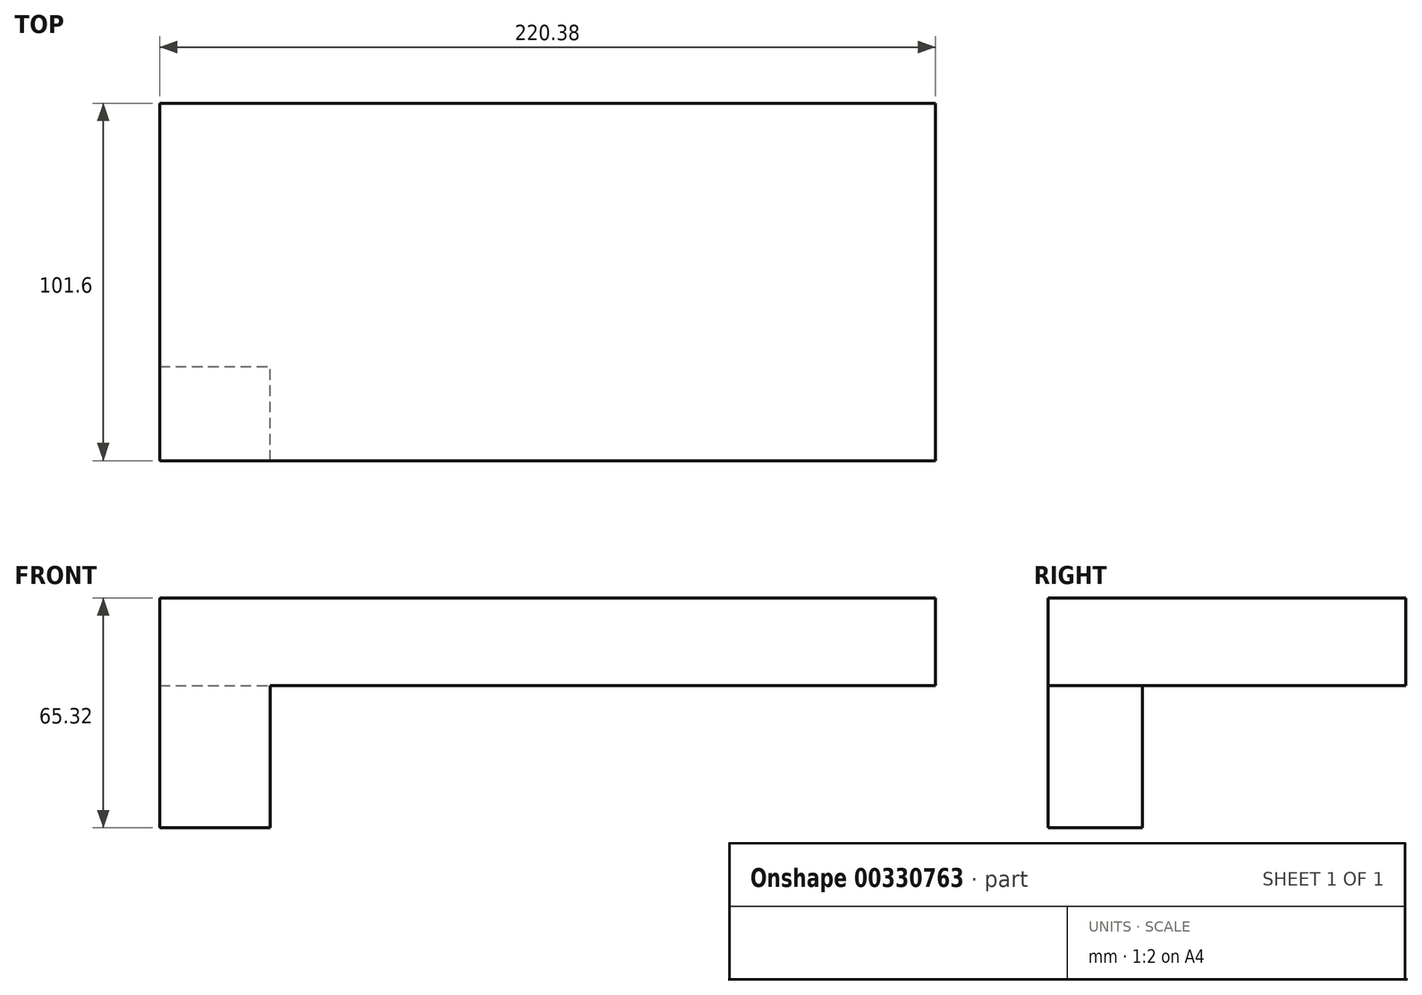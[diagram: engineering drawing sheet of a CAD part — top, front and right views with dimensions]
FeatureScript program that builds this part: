
annotation { "Feature Type Name" : "Feature", "Feature Type Description" : "" }
export const myFeature = defineFeature(function(context is Context, id is Id, definition is map)
    precondition{}
    {
        {
            var Q0;
            Q0=qCreatedBy(makeId("Front.planeOp"),FACE);
            var sketch = newSketch(context, id + "F0", { "sketchPlane" : qUnion([Q0])});
            skLineSegment(sketch, "E0.bottom", {"start": v(59.4, 12.46) * mm, "end": v(-59.4, 12.46) * mm});
            skLineSegment(sketch, "E0.top", {"start": v(59.4, -12.46) * mm, "end": v(-59.4, -12.46) * mm});
            skLineSegment(sketch, "E0.left", {"start": v(59.4, 12.46) * mm, "end": v(59.4, -12.46) * mm});
            skLineSegment(sketch, "E0.right", {"start": v(-59.4, 12.46) * mm, "end": v(-59.4, -12.46) * mm});
            skPoint(sketch, "E0.middle", {"position": v(0, 0) * mm});
            skSolve(sketch);
        }
        {
            var Q0;
            Q0=makeQuery(id+"F0.imprint","IMPRINT",FACE,{"disambiguationData":[TD([[makeQuery(id+"F0.imprint","IMPRINT",EDGE,{"derivedFrom":sQuery(id+"F0.wireOp",EDGE,"E0.bottom")}),1.0]])]});
            extrude(context, id + "F1", {"entities" : qUnion([Q0]), "depth" : 25.4 * mm});
        }
        {
            var Q0;
            Q0=makeQuery(id+"F1.opExtrude","CAP_FACE",FACE,{"disambiguationData":[OSD([sQuery(id+"F0.wireOp",EDGE,"E0.bottom"),sQuery(id+"F0.wireOp",EDGE,"E0.top"),sQuery(id+"F0.wireOp",EDGE,"E0.left"),sQuery(id+"F0.wireOp",EDGE,"E0.right")])],"isStart":true});
            extrude(context, id + "F2", {"entities" : qUnion([Q0]), "operationType" : NewBodyOperationType.ADD, "depth" : 25.4 * mm});
        }
        {
            var Q0;
            {var subQ0=sQuery(id+"F0.wireOp",EDGE,"E0.right");Q0=makeQuery(id+"F2.boolean.opBoolean","MERGE",FACE,{"derivedFrom":[makeQuery(id+"F1.opExtrude","SWEPT_FACE",FACE,{"disambiguationData":[OSD([subQ0])]}),makeQuery(id+"F2.opExtrude","SWEPT_FACE",FACE,{"disambiguationData":[OSD([subQ0])]})]});}
            extrude(context, id + "F3", {"entities" : qUnion([Q0]), "operationType" : NewBodyOperationType.ADD, "depth" : 25.4 * mm});
        }
        {
            var Q0;
            {var subQ0=sQuery(id+"F0.wireOp",EDGE,"E0.left");Q0=makeQuery(id+"F2.boolean.opBoolean","MERGE",FACE,{"derivedFrom":[makeQuery(id+"F1.opExtrude","SWEPT_FACE",FACE,{"disambiguationData":[OSD([subQ0])]}),makeQuery(id+"F2.opExtrude","SWEPT_FACE",FACE,{"disambiguationData":[OSD([subQ0])]})]});}
            extrude(context, id + "F4", {"entities" : qUnion([Q0]), "operationType" : NewBodyOperationType.ADD, "depth" : 25.4 * mm});
        }
        {
            var Q0;
            Q0=makeQuery(id+"F4.opExtrude","CAP_FACE",FACE,{"disambiguationData":[OSD([sQuery(id+"F0.wireOp",EDGE,"E0.left")])],"isStart":false});
            extrude(context, id + "F5", {"entities" : qUnion([Q0]), "operationType" : NewBodyOperationType.ADD, "depth" : 25.4 * mm});
        }
        {
            var Q0;
            Q0=makeQuery(id+"F3.opExtrude","CAP_FACE",FACE,{"disambiguationData":[OSD([sQuery(id+"F0.wireOp",EDGE,"E0.right")])],"isStart":false});
            extrude(context, id + "F6", {"entities" : qUnion([Q0]), "operationType" : NewBodyOperationType.ADD, "depth" : 25.4 * mm});
        }
        {
            var Q0;
            {var subQ0=sQuery(id+"F0.wireOp",EDGE,"E0.right");var subQ1=makeQuery(id+"F1.opExtrude","CAP_EDGE",EDGE,{"disambiguationData":[OSD([subQ0])],"isStart":false});var subQ2=sQuery(id+"F0.wireOp",EDGE,"E0.left");var subQ3=makeQuery(id+"F1.opExtrude","CAP_EDGE",EDGE,{"disambiguationData":[OSD([subQ2])],"isStart":false});Q0=makeQuery(id+"F6.boolean.opBoolean","MERGE",FACE,{"derivedFrom":[makeQuery(id+"F5.boolean.opBoolean","MERGE",FACE,{"derivedFrom":[makeQuery(id+"F4.boolean.opBoolean","MERGE",FACE,{"derivedFrom":[makeQuery(id+"F3.boolean.opBoolean","MERGE",FACE,{"derivedFrom":[makeQuery(id+"F1.opExtrude","CAP_FACE",FACE,{"disambiguationData":[OSD([sQuery(id+"F0.wireOp",EDGE,"E0.bottom"),sQuery(id+"F0.wireOp",EDGE,"E0.top"),subQ2,subQ0])],"isStart":false}),makeQuery(id+"F3.opExtrude","SWEPT_FACE",FACE,{"disambiguationData":[OSD([subQ0]),TDD([subQ1])]})]}),makeQuery(id+"F4.opExtrude","SWEPT_FACE",FACE,{"disambiguationData":[OSD([subQ2]),TDD([subQ3])]})]}),makeQuery(id+"F5.opExtrude","SWEPT_FACE",FACE,{"disambiguationData":[OSD([subQ2]),TDD([makeQuery(id+"F4.opExtrude","CAP_EDGE",EDGE,{"disambiguationData":[OSD([subQ2]),TDD([subQ3])],"isStart":false})])]})]}),makeQuery(id+"F6.opExtrude","SWEPT_FACE",FACE,{"disambiguationData":[OSD([subQ0]),TDD([makeQuery(id+"F3.opExtrude","CAP_EDGE",EDGE,{"disambiguationData":[OSD([subQ0]),TDD([subQ1])],"isStart":false})])]})]});}
            extrude(context, id + "F7", {"entities" : qUnion([Q0]), "operationType" : NewBodyOperationType.ADD, "depth" : 25.4 * mm});
        }
        {
            var Q0;
            {var subQ0=sQuery(id+"F0.wireOp",EDGE,"E0.right");var subQ1=makeQuery(id+"F2.opExtrude","CAP_EDGE",EDGE,{"disambiguationData":[OSD([subQ0])],"isStart":false});var subQ2=sQuery(id+"F0.wireOp",EDGE,"E0.left");var subQ3=makeQuery(id+"F2.opExtrude","CAP_EDGE",EDGE,{"disambiguationData":[OSD([subQ2])],"isStart":false});Q0=makeQuery(id+"F6.boolean.opBoolean","MERGE",FACE,{"derivedFrom":[makeQuery(id+"F5.boolean.opBoolean","MERGE",FACE,{"derivedFrom":[makeQuery(id+"F4.boolean.opBoolean","MERGE",FACE,{"derivedFrom":[makeQuery(id+"F3.boolean.opBoolean","MERGE",FACE,{"derivedFrom":[makeQuery(id+"F2.opExtrude","CAP_FACE",FACE,{"disambiguationData":[OSD([sQuery(id+"F0.wireOp",EDGE,"E0.bottom"),sQuery(id+"F0.wireOp",EDGE,"E0.top"),subQ2,subQ0])],"isStart":false}),makeQuery(id+"F3.opExtrude","SWEPT_FACE",FACE,{"disambiguationData":[OSD([subQ0]),TDD([subQ1])]})]}),makeQuery(id+"F4.opExtrude","SWEPT_FACE",FACE,{"disambiguationData":[OSD([subQ2]),TDD([subQ3])]})]}),makeQuery(id+"F5.opExtrude","SWEPT_FACE",FACE,{"disambiguationData":[OSD([subQ2]),TDD([makeQuery(id+"F4.opExtrude","CAP_EDGE",EDGE,{"disambiguationData":[OSD([subQ2]),TDD([subQ3])],"isStart":false})])]})]}),makeQuery(id+"F6.opExtrude","SWEPT_FACE",FACE,{"disambiguationData":[OSD([subQ0]),TDD([makeQuery(id+"F3.opExtrude","CAP_EDGE",EDGE,{"disambiguationData":[OSD([subQ0]),TDD([subQ1])],"isStart":false})])]})]});}
            extrude(context, id + "F8", {"entities" : qUnion([Q0]), "operationType" : NewBodyOperationType.ADD, "depth" : 25.4 * mm});
        }
        {
            var Q0;
            {var subQ0=sQuery(id+"F0.wireOp",EDGE,"E0.right");var subQ1=sQuery(id+"F0.wireOp",EDGE,"E0.left");var subQ2=sQuery(id+"F0.wireOp",EDGE,"E0.bottom");Q0=makeQuery(id+"F8.boolean.opBoolean","MERGE",FACE,{"derivedFrom":[makeQuery(id+"F7.boolean.opBoolean","MERGE",FACE,{"derivedFrom":[makeQuery(id+"F6.boolean.opBoolean","MERGE",FACE,{"derivedFrom":[makeQuery(id+"F5.boolean.opBoolean","MERGE",FACE,{"derivedFrom":[makeQuery(id+"F4.boolean.opBoolean","MERGE",FACE,{"derivedFrom":[makeQuery(id+"F3.boolean.opBoolean","MERGE",FACE,{"derivedFrom":[makeQuery(id+"F2.boolean.opBoolean","MERGE",FACE,{"derivedFrom":[makeQuery(id+"F1.opExtrude","SWEPT_FACE",FACE,{"disambiguationData":[OSD([subQ2])]}),makeQuery(id+"F2.opExtrude","SWEPT_FACE",FACE,{"disambiguationData":[OSD([subQ2])]})]}),makeQuery(id+"F3.opExtrude","SWEPT_FACE",FACE,{"disambiguationData":[OSD([subQ2,subQ0])]})]}),makeQuery(id+"F4.opExtrude","SWEPT_FACE",FACE,{"disambiguationData":[OSD([subQ2,subQ1])]})]}),makeQuery(id+"F5.opExtrude","SWEPT_FACE",FACE,{"disambiguationData":[OSD([subQ2,subQ1])]})]}),makeQuery(id+"F6.opExtrude","SWEPT_FACE",FACE,{"disambiguationData":[OSD([subQ2,subQ0])]})]}),makeQuery(id+"F7.opExtrude","SWEPT_FACE",FACE,{"disambiguationData":[OSD([subQ2,subQ1,subQ0])]})]}),makeQuery(id+"F8.opExtrude","SWEPT_FACE",FACE,{"disambiguationData":[OSD([subQ2,subQ1,subQ0])]})]});}
            var sketch = newSketch(context, id + "F9", { "sketchPlane" : qUnion([Q0])});
            skFitSpline(sketch, "E1", {"points": [v(-110.2, -25.26) * mm, v(-39.39, 0) * mm, v(25.26, -31.68) * mm, v(110.2, 0) * mm], "startDerivative": vector(223.96, 137.2) * mm, "endDerivative": vector(248.73, 153.96) * mm});
            skSolve(sketch);
        }
        {
            var Q0;
            {var subQ0=sQuery(id+"F0.wireOp",EDGE,"E0.right");var subQ1=sQuery(id+"F0.wireOp",EDGE,"E0.left");var subQ2=sQuery(id+"F0.wireOp",EDGE,"E0.top");Q0=makeQuery(id+"F8.boolean.opBoolean","MERGE",FACE,{"derivedFrom":[makeQuery(id+"F7.boolean.opBoolean","MERGE",FACE,{"derivedFrom":[makeQuery(id+"F6.boolean.opBoolean","MERGE",FACE,{"derivedFrom":[makeQuery(id+"F5.boolean.opBoolean","MERGE",FACE,{"derivedFrom":[makeQuery(id+"F4.boolean.opBoolean","MERGE",FACE,{"derivedFrom":[makeQuery(id+"F3.boolean.opBoolean","MERGE",FACE,{"derivedFrom":[makeQuery(id+"F2.boolean.opBoolean","MERGE",FACE,{"derivedFrom":[makeQuery(id+"F1.opExtrude","SWEPT_FACE",FACE,{"disambiguationData":[OSD([subQ2])]}),makeQuery(id+"F2.opExtrude","SWEPT_FACE",FACE,{"disambiguationData":[OSD([subQ2])]})]}),makeQuery(id+"F3.opExtrude","SWEPT_FACE",FACE,{"disambiguationData":[OSD([subQ2,subQ0])]})]}),makeQuery(id+"F4.opExtrude","SWEPT_FACE",FACE,{"disambiguationData":[OSD([subQ2,subQ1])]})]}),makeQuery(id+"F5.opExtrude","SWEPT_FACE",FACE,{"disambiguationData":[OSD([subQ2,subQ1])]})]}),makeQuery(id+"F6.opExtrude","SWEPT_FACE",FACE,{"disambiguationData":[OSD([subQ2,subQ0])]})]}),makeQuery(id+"F7.opExtrude","SWEPT_FACE",FACE,{"disambiguationData":[OSD([subQ2,subQ1,subQ0])]})]}),makeQuery(id+"F8.opExtrude","SWEPT_FACE",FACE,{"disambiguationData":[OSD([subQ2,subQ1,subQ0])]})]});}
            var sketch = newSketch(context, id + "F10", { "sketchPlane" : qUnion([Q0])});
            skLineSegment(sketch, "E2.bottom", {"start": v(-110.2, 50.8) * mm, "end": v(-78.8, 50.8) * mm});
            skLineSegment(sketch, "E2.top", {"start": v(-110.2, 24.02) * mm, "end": v(-78.8, 24.02) * mm});
            skLineSegment(sketch, "E2.left", {"start": v(-110.2, 50.8) * mm, "end": v(-110.2, 24.02) * mm});
            skLineSegment(sketch, "E2.right", {"start": v(-78.8, 50.8) * mm, "end": v(-78.8, 24.02) * mm});
            skSolve(sketch);
        }
        {
            var Q0;
            Q0=makeQuery(id+"F10.imprint","IMPRINT",FACE,{"disambiguationData":[TD([[makeQuery(id+"F10.imprint","IMPRINT",EDGE,{"derivedFrom":sQuery(id+"F10.wireOp",EDGE,"E2.bottom")}),1.0]])]});
            var sketch = newSketch(context, id + "F11", { "sketchPlane" : qUnion([Q0])});
            skSolve(sketch);
        }
        {
            var Q0;
            Q0 = qSketchRegion(id + "F11", true);
            var Q1;
            Q1=makeQuery(id+"F11.imprint","IMPRINT",FACE,{"disambiguationData":[TD([[makeQuery(id+"F11.imprint","IMPRINT",EDGE,{"derivedFrom":makeQuery(id+"F10.imprint","IMPRINT",EDGE,{"derivedFrom":sQuery(id+"F10.wireOp",EDGE,"E2.bottom")})}),1.0]])]});
            extrude(context, id + "F12", {"entities" : qUnion([Q0, Q1]), "operationType" : NewBodyOperationType.ADD, "depth" : 40.4 * mm});
        }
    });
